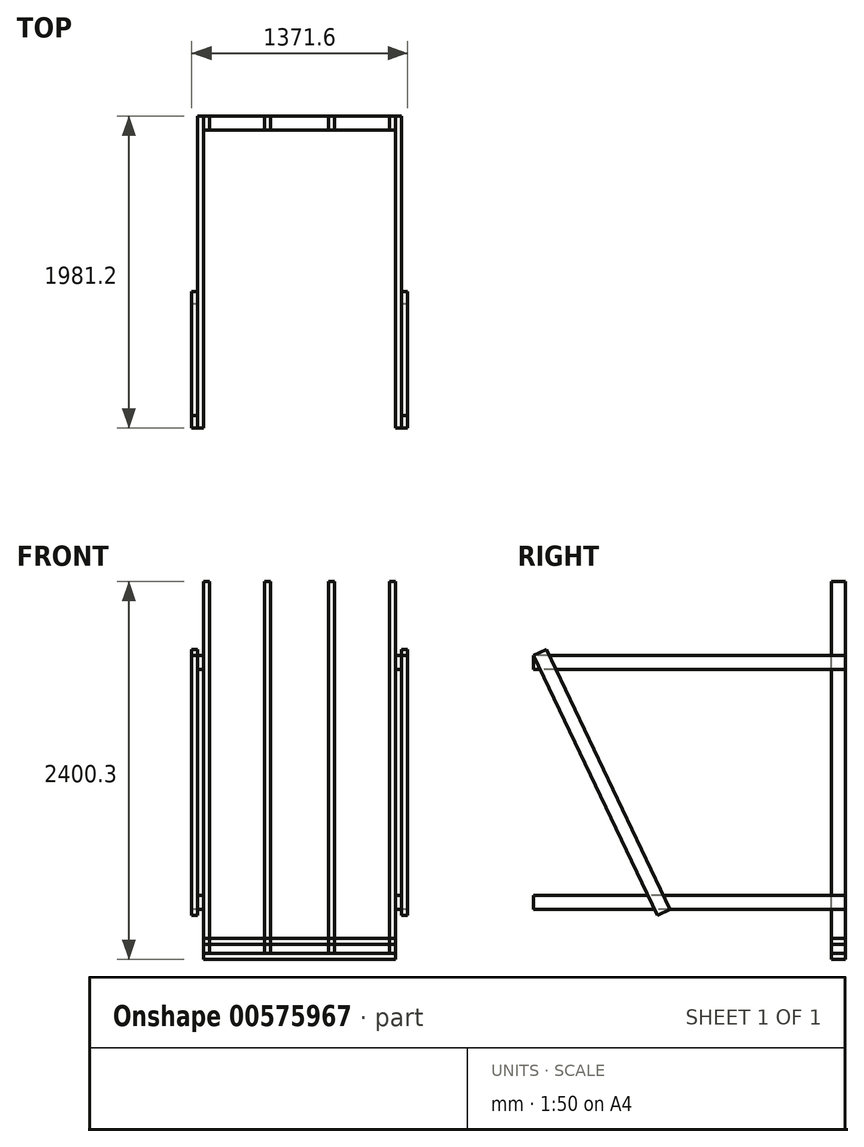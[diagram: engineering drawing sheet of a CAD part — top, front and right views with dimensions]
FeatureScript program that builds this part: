
annotation { "Feature Type Name" : "Feature", "Feature Type Description" : "" }
export const myFeature = defineFeature(function(context is Context, id is Id, definition is map)
    precondition{}
    {
        {
            var Q0;
            Q0=qCreatedBy(makeId("Front.planeOp"),FACE);
            var sketch = newSketch(context, id + "F0", { "sketchPlane" : qUnion([Q0])});
            skLineSegment(sketch, "E0.bottom", {"start": v(0, 0) * mm, "end": v(38.1, 0) * mm});
            skLineSegment(sketch, "E0.top", {"start": v(0, 2362.2) * mm, "end": v(38.1, 2362.2) * mm});
            skLineSegment(sketch, "E0.left", {"start": v(0, 0) * mm, "end": v(0, 2362.2) * mm});
            skLineSegment(sketch, "E0.right", {"start": v(38.1, 0) * mm, "end": v(38.1, 2362.2) * mm});
            skSolve(sketch);
        }
        {
            var Q0;
            Q0=qSketchRegion(id+"F0",true);
            extrude(context, id + "F1", {"entities" : qUnion([Q0]), "depth" : 88.9 * mm, "offsetDistance" : 25.4 * mm});
        }
        {
            var Q0;
            Q0=makeQuery(id+"F1.opExtrude","SWEPT_BODY",BODY,{"disambiguationData":[OSD([sQuery(id+"F0.wireOp",EDGE,"E0.bottom"),sQuery(id+"F0.wireOp",EDGE,"E0.top"),sQuery(id+"F0.wireOp",EDGE,"E0.left"),sQuery(id+"F0.wireOp",EDGE,"E0.right")])]});
            transform(context, id + "F2", {"entities" : qUnion([Q0]), "transformType" : TransformType.TRANSLATION_3D, "dx" : 387.35 * mm, "dy" : 0 * mm, "dz" : 0 * mm, "makeCopy" : true});
        }
        {
            var Q0;
            Q0=makeQuery(id+"F2.opPattern","COPY",BODY,{"derivedFrom":makeQuery(id+"F1.opExtrude","SWEPT_BODY",BODY,{"disambiguationData":[OSD([sQuery(id+"F0.wireOp",EDGE,"E0.bottom"),sQuery(id+"F0.wireOp",EDGE,"E0.top"),sQuery(id+"F0.wireOp",EDGE,"E0.left"),sQuery(id+"F0.wireOp",EDGE,"E0.right")])]}),"instanceName":"1"});
            transform(context, id + "F3", {"entities" : qUnion([Q0]), "transformType" : TransformType.TRANSLATION_3D, "dx" : 406.4 * mm, "dy" : 0 * mm, "dz" : 0 * mm, "makeCopy" : true});
        }
        {
            var Q0;
            Q0=makeQuery(id+"F3.opPattern","COPY",BODY,{"derivedFrom":makeQuery(id+"F2.opPattern","COPY",BODY,{"derivedFrom":makeQuery(id+"F1.opExtrude","SWEPT_BODY",BODY,{"disambiguationData":[OSD([sQuery(id+"F0.wireOp",EDGE,"E0.bottom"),sQuery(id+"F0.wireOp",EDGE,"E0.top"),sQuery(id+"F0.wireOp",EDGE,"E0.left"),sQuery(id+"F0.wireOp",EDGE,"E0.right")])]}),"instanceName":"1"}),"instanceName":"1"});
            transform(context, id + "F4", {"entities" : qUnion([Q0]), "transformType" : TransformType.TRANSLATION_3D, "dx" : 387.35 * mm, "dy" : 0 * mm, "dz" : 0 * mm, "makeCopy" : true});
        }
        {
            var Q0;
            Q0=qCreatedBy(makeId("Front.planeOp"),FACE);
            var sketch = newSketch(context, id + "F5", { "sketchPlane" : qUnion([Q0])});
            skLineSegment(sketch, "E1.bottom", {"start": v(0, 0) * mm, "end": v(1219.2, 0) * mm});
            skLineSegment(sketch, "E1.top", {"start": v(0, -38.1) * mm, "end": v(1219.2, -38.1) * mm});
            skLineSegment(sketch, "E1.left", {"start": v(0, 0) * mm, "end": v(0, -38.1) * mm});
            skLineSegment(sketch, "E1.right", {"start": v(1219.2, 0) * mm, "end": v(1219.2, -38.1) * mm});
            skSolve(sketch);
        }
        {
            var Q0;
            Q0=qSketchRegion(id+"F5",true);
            extrude(context, id + "F6", {"entities" : qUnion([Q0]), "depth" : 88.9 * mm, "offsetDistance" : 25.4 * mm});
        }
        {
            var Q0;
            Q0=makeQuery(id+"F6.opExtrude","SWEPT_BODY",BODY,{"disambiguationData":[OSD([sQuery(id+"F5.wireOp",EDGE,"E1.bottom"),sQuery(id+"F5.wireOp",EDGE,"E1.top"),sQuery(id+"F5.wireOp",EDGE,"E1.left"),sQuery(id+"F5.wireOp",EDGE,"E1.right")])]});
            transform(context, id + "F7", {"entities" : qUnion([Q0]), "transformType" : TransformType.TRANSLATION_3D, "dx" : 0 * mm, "dy" : 0 * mm, "dz" : ((8 * 12) - 1.5) * mm, "makeCopy" : true});
        }
        {
            var Q0;
            Q0=makeQuery(id+"F6.opExtrude","SWEPT_FACE",FACE,{"disambiguationData":[OSD([sQuery(id+"F5.wireOp",EDGE,"E1.left")])]});
            var sketch = newSketch(context, id + "F8", { "sketchPlane" : qUnion([Q0])});
            skLineSegment(sketch, "E2.bottom", {"start": v(958.85, 50.8) * mm, "end": v(-869.95, 50.8) * mm});
            skLineSegment(sketch, "E2.top", {"start": v(958.85, -38.1) * mm, "end": v(-869.95, -38.1) * mm});
            skLineSegment(sketch, "E2.left", {"start": v(958.85, 50.8) * mm, "end": v(958.85, -38.1) * mm});
            skLineSegment(sketch, "E2.right", {"start": v(-869.95, 50.8) * mm, "end": v(-869.95, -38.1) * mm});
            skSolve(sketch);
        }
        {
            var Q0;
            Q0=qSketchRegion(id+"F8",true);
            extrude(context, id + "F9", {"entities" : qUnion([Q0]), "depth" : 38.1 * mm, "offsetDistance" : 25.4 * mm});
        }
        {
            var Q0;
            Q0=makeQuery(id+"F9.opExtrude","SWEPT_BODY",BODY,{"disambiguationData":[OSD([sQuery(id+"F8.wireOp",EDGE,"E2.bottom"),sQuery(id+"F8.wireOp",EDGE,"E2.top"),sQuery(id+"F8.wireOp",EDGE,"E2.left"),sQuery(id+"F8.wireOp",EDGE,"E2.right")])]});
            transform(context, id + "F10", {"entities" : qUnion([Q0]), "transformType" : TransformType.TRANSLATION_3D, "dx" : 1257.3 * mm, "dy" : 0 * mm, "dz" : 0 * mm, "makeCopy" : true});
        }
        {
            var Q0;
            Q0=makeQuery(id+"F10.opPattern","COPY",FACE,{"derivedFrom":makeQuery(id+"F9.opExtrude","CAP_FACE",FACE,{"disambiguationData":[OSD([sQuery(id+"F8.wireOp",EDGE,"E2.bottom"),sQuery(id+"F8.wireOp",EDGE,"E2.top"),sQuery(id+"F8.wireOp",EDGE,"E2.left"),sQuery(id+"F8.wireOp",EDGE,"E2.right")])],"isStart":false}),"instanceName":"1"});
            var sketch = newSketch(context, id + "F11", { "sketchPlane" : qUnion([Q0])});
            skLineSegment(sketch, "E3", {"start": v(-825.5, 50.8) * mm, "end": v(0, 1480.6) * mm});
            skLineSegment(sketch, "E4", {"start": v(0, 1480.6) * mm, "end": v(0, 1302.8) * mm});
            skLineSegment(sketch, "E5", {"start": v(0, 1302.8) * mm, "end": v(-722.85, 50.8) * mm});
            skLineSegment(sketch, "E6", {"start": v(-825.5, 50.8) * mm, "end": v(-722.85, 50.8) * mm});
            skLineSegment(sketch, "E7", {"start": v(0, 1480.6) * mm, "end": v(88.9, 1634.59) * mm});
            skLineSegment(sketch, "E8", {"start": v(0, 1302.8) * mm, "end": v(88.9, 1456.79) * mm});
            skLineSegment(sketch, "E9", {"start": v(88.9, 1634.59) * mm, "end": v(88.9, 1456.79) * mm});
            skSolve(sketch);
        }
        {
            var Q0;
            Q0=qSketchRegion(id+"F11",true);
            extrude(context, id + "F12", {"entities" : qUnion([Q0]), "oppositeDirection" : true, "depth" : 38.1 * mm, "offsetDistance" : 25.4 * mm});
        }
        {
            var Q0;
            Q0=makeQuery(id+"F12.opExtrude","SWEPT_BODY",BODY,{"disambiguationData":[OSD([sQuery(id+"F11.wireOp",EDGE,"E3"),sQuery(id+"F11.wireOp",EDGE,"E4"),sQuery(id+"F11.wireOp",EDGE,"E5"),sQuery(id+"F11.wireOp",EDGE,"1W0fkmu6-52x2-68E4-ANrA-ky8dyzSj9vcL")])]});
            transform(context, id + "F13", {"entities" : qUnion([Q0]), "transformType" : TransformType.TRANSLATION_3D, "dx" : -1257.3 * mm, "dy" : 0 * mm, "dz" : 0 * mm, "makeCopy" : true});
        }
        {
            var Q0;
            Q0=qCreatedBy(makeId("Right.planeOp"),FACE);
            var sketch = newSketch(context, id + "F14", { "sketchPlane" : qUnion([Q0])});
            skLineSegment(sketch, "E10.bottom", {"start": v(0, 1803.4) * mm, "end": v(-1981.2, 1803.4) * mm});
            skLineSegment(sketch, "E10.top", {"start": v(0, 1892.3) * mm, "end": v(-1981.2, 1892.3) * mm});
            skLineSegment(sketch, "E10.left", {"start": v(0, 1803.4) * mm, "end": v(0, 1892.3) * mm});
            skLineSegment(sketch, "E10.right", {"start": v(-1981.2, 1803.4) * mm, "end": v(-1981.2, 1892.3) * mm});
            skSolve(sketch);
        }
        {
            var Q0;
            Q0=qSketchRegion(id+"F14",true);
            extrude(context, id + "F15", {"entities" : qUnion([Q0]), "oppositeDirection" : true, "depth" : 38.1 * mm, "offsetDistance" : 25.4 * mm});
        }
        {
            var Q0;
            Q0=makeQuery(id+"F15.opExtrude","SWEPT_BODY",BODY,{"disambiguationData":[OSD([sQuery(id+"F14.wireOp",EDGE,"E10.bottom"),sQuery(id+"F14.wireOp",EDGE,"E10.top"),sQuery(id+"F14.wireOp",EDGE,"E10.left"),sQuery(id+"F14.wireOp",EDGE,"E10.right")])]});
            transform(context, id + "F16", {"entities" : qUnion([Q0]), "transformType" : TransformType.TRANSLATION_3D, "dx" : 1257.3 * mm, "dy" : 0 * mm, "dz" : 0 * mm, "makeCopy" : true});
        }
        {
            var Q0;
            Q0=makeQuery(id+"F15.opExtrude","SWEPT_BODY",BODY,{"disambiguationData":[OSD([sQuery(id+"F14.wireOp",EDGE,"E10.bottom"),sQuery(id+"F14.wireOp",EDGE,"E10.top"),sQuery(id+"F14.wireOp",EDGE,"E10.left"),sQuery(id+"F14.wireOp",EDGE,"E10.right")])]});
            transform(context, id + "F17", {"entities" : qUnion([Q0]), "transformType" : TransformType.TRANSLATION_3D, "dx" : 0 * mm, "dy" : 0 * mm, "dz" : -1524 * mm, "makeCopy" : true});
        }
        {
            var Q0;
            Q0=makeQuery(id+"F17.opPattern","COPY",BODY,{"derivedFrom":makeQuery(id+"F15.opExtrude","SWEPT_BODY",BODY,{"disambiguationData":[OSD([sQuery(id+"F14.wireOp",EDGE,"E10.bottom"),sQuery(id+"F14.wireOp",EDGE,"E10.top"),sQuery(id+"F14.wireOp",EDGE,"E10.left"),sQuery(id+"F14.wireOp",EDGE,"E10.right")])]}),"instanceName":"1"});
            transform(context, id + "F18", {"entities" : qUnion([Q0]), "transformType" : TransformType.TRANSLATION_3D, "dx" : 1257.3 * mm, "dy" : 0 * mm, "dz" : 0 * mm, "makeCopy" : true});
        }
        {
            var Q0;
            Q0=makeQuery(id+"F18.opPattern","COPY",FACE,{"derivedFrom":makeQuery(id+"F17.opPattern","COPY",FACE,{"derivedFrom":makeQuery(id+"F15.opExtrude","CAP_FACE",FACE,{"disambiguationData":[OSD([sQuery(id+"F14.wireOp",EDGE,"E10.bottom"),sQuery(id+"F14.wireOp",EDGE,"E10.top"),sQuery(id+"F14.wireOp",EDGE,"E10.left"),sQuery(id+"F14.wireOp",EDGE,"E10.right")])],"isStart":true}),"instanceName":"1"}),"instanceName":"1"});
            var sketch = newSketch(context, id + "F19", { "sketchPlane" : qUnion([Q0])});
            skLineSegment(sketch, "E11", {"start": v(-1900.94, 1930.52) * mm, "end": v(-1114.62, 279.4) * mm});
            skLineSegment(sketch, "E12", {"start": v(-1114.62, 279.4) * mm, "end": v(-1194.88, 241.18) * mm});
            skLineSegment(sketch, "E13", {"start": v(-1981.2, 1892.3) * mm, "end": v(-1194.88, 241.18) * mm});
            skLineSegment(sketch, "E14", {"start": v(-1900.94, 1930.52) * mm, "end": v(-1981.2, 1892.3) * mm});
            skSolve(sketch);
        }
        {
            var Q0;
            Q0=qSketchRegion(id+"F19",true);
            extrude(context, id + "F20", {"entities" : qUnion([Q0]), "depth" : 38.1 * mm, "offsetDistance" : 25.4 * mm});
        }
        {
            var Q0;
            Q0=makeQuery(id+"F20.opExtrude","SWEPT_BODY",BODY,{"disambiguationData":[OSD([sQuery(id+"F19.wireOp",EDGE,"E11"),sQuery(id+"F19.wireOp",EDGE,"E12"),sQuery(id+"F19.wireOp",EDGE,"E13"),sQuery(id+"F19.wireOp",EDGE,"E14")])]});
            transform(context, id + "F21", {"entities" : qUnion([Q0]), "transformType" : TransformType.TRANSLATION_3D, "dx" : -1333.5 * mm, "dy" : 0 * mm, "dz" : 0 * mm, "makeCopy" : true});
        }
        {
            var Q0;
            Q0=makeQuery(id+"F9.opExtrude","SWEPT_BODY",BODY,{"disambiguationData":[OSD([sQuery(id+"F8.wireOp",EDGE,"E2.bottom"),sQuery(id+"F8.wireOp",EDGE,"E2.top"),sQuery(id+"F8.wireOp",EDGE,"E2.left"),sQuery(id+"F8.wireOp",EDGE,"E2.right")])]});
            deleteBodies(context, id + "F22", {"entities" : qUnion([Q0])});
        }
        {
            var Q0;
            Q0=makeQuery(id+"F10.opPattern","COPY",BODY,{"derivedFrom":makeQuery(id+"F9.opExtrude","SWEPT_BODY",BODY,{"disambiguationData":[OSD([sQuery(id+"F8.wireOp",EDGE,"E2.bottom"),sQuery(id+"F8.wireOp",EDGE,"E2.top"),sQuery(id+"F8.wireOp",EDGE,"E2.left"),sQuery(id+"F8.wireOp",EDGE,"E2.right")])]}),"instanceName":"1"});
            deleteBodies(context, id + "F23", {"entities" : qUnion([Q0])});
        }
        {
            var Q0;
            Q0=makeQuery(id+"F12.opExtrude","SWEPT_BODY",BODY,{"disambiguationData":[OSD([sQuery(id+"F11.wireOp",EDGE,"E3"),sQuery(id+"F11.wireOp",EDGE,"E5"),sQuery(id+"F11.wireOp",EDGE,"E6"),sQuery(id+"F11.wireOp",EDGE,"E7"),sQuery(id+"F11.wireOp",EDGE,"E8"),sQuery(id+"F11.wireOp",EDGE,"E9")])]});
            deleteBodies(context, id + "F24", {"entities" : qUnion([Q0])});
        }
        {
            var Q0;
            Q0=makeQuery(id+"F13.opPattern","COPY",BODY,{"derivedFrom":makeQuery(id+"F12.opExtrude","SWEPT_BODY",BODY,{"disambiguationData":[OSD([sQuery(id+"F11.wireOp",EDGE,"E3"),sQuery(id+"F11.wireOp",EDGE,"E5"),sQuery(id+"F11.wireOp",EDGE,"E6"),sQuery(id+"F11.wireOp",EDGE,"E7"),sQuery(id+"F11.wireOp",EDGE,"E8"),sQuery(id+"F11.wireOp",EDGE,"E9")])]}),"instanceName":"1"});
            deleteBodies(context, id + "F25", {"entities" : qUnion([Q0])});
        }
    });
